annotation { "Feature Type Name" : "Feature", "Feature Type Description" : "" }
export const myFeature = defineFeature(function(context is Context, id is Id, definition is map)
    precondition{}
    {
        {
            var Q0;
            Q0=qCreatedBy(makeId("Front.planeOp"),FACE);
            var sketch = newSketch(context, id + "F0", { "sketchPlane" : qUnion([Q0])});
            skLineSegment(sketch, "E0.bottom", {"start": v(3.18, 0) * mm, "end": v(85.72, 0) * mm});
            skLineSegment(sketch, "E0.top", {"start": v(3.17, 50.8) * mm, "end": v(85.73, 50.8) * mm});
            skLineSegment(sketch, "E0.left", {"start": v(0, 3.18) * mm, "end": v(0, 47.62) * mm});
            skLineSegment(sketch, "E0.right", {"start": v(88.9, 3.18) * mm, "end": v(88.9, 47.62) * mm});
            skPoint(sketch, "E1.visualSharp", {"position": v(0, 50.8) * mm});
            skArc(sketch, "E1.filletArc", {"start": v(3.17, 50.8) * mm, "mid": v(0.93, 49.87) * mm, "end": v(0, 47.62) * mm});
            skPoint(sketch, "E2.visualSharp", {"position": v(88.9, 50.8) * mm});
            skArc(sketch, "E2.filletArc", {"start": v(88.9, 47.62) * mm, "mid": v(87.97, 49.87) * mm, "end": v(85.73, 50.8) * mm});
            skPoint(sketch, "E3.visualSharp", {"position": v(88.9, 0) * mm});
            skArc(sketch, "E3.filletArc", {"start": v(85.73, 0) * mm, "mid": v(87.97, 0.93) * mm, "end": v(88.9, 3.18) * mm});
            skPoint(sketch, "E4.visualSharp", {"position": v(0, 0) * mm});
            skArc(sketch, "E4.filletArc", {"start": v(0, 3.17) * mm, "mid": v(0.93, 0.93) * mm, "end": v(3.18, 0) * mm});
            skSolve(sketch);
        }
        {
            var Q0;
            Q0 = qSketchRegion(id + "F0", true);
            extrude(context, id + "F1", {"entities" : qUnion([Q0]), "depth" : 0.64 * mm});
        }
        {
            var Q0;
            Q0=makeQuery(id+"F1.opExtrude","CAP_FACE",FACE,{"disambiguationData":[OSD([sQuery(id+"F0.wireOp",EDGE,"E0.bottom"),sQuery(id+"F0.wireOp",EDGE,"E0.top"),sQuery(id+"F0.wireOp",EDGE,"E0.left"),sQuery(id+"F0.wireOp",EDGE,"E0.right")])],"isStart":false});
            var sketch = newSketch(context, id + "F2", { "sketchPlane" : qUnion([Q0])});
            skText(sketch, "E5", { "text": "Dan Haber", "fontName": "AllertaStencil-Regular.ttf"});
            skText(sketch, "E6", { "text": "All-around person", "fontName": "AllertaStencil-Regular.ttf"});
            const initialGuessF2  = {"E5": [0.00348, 0.03585, 1, 0, 0.0104], "E6": [0.00381, 0.0238, 1, 0, 0.00546]};
            skSetInitialGuess(sketch, initialGuessF2);
            skSolve(sketch);
        }
        {
            var Q0;
            Q0 = qSketchRegion(id + "F2", true);
            extrude(context, id + "F3", {"entities" : qUnion([Q0]), "operationType" : NewBodyOperationType.REMOVE, "oppositeDirection" : true, "depth" : 25.4 * mm});
        }
    });